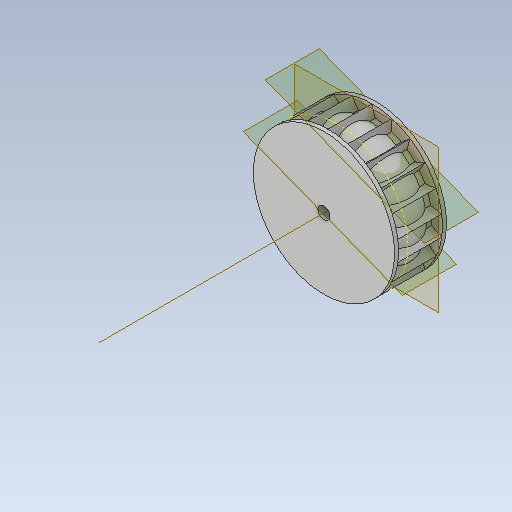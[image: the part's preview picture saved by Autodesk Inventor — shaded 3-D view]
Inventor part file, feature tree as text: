
AUTODESK INVENTOR PART (.ipt)
format: ipt  version: 2020 (Build 240168000, 168)  size: 521,216 bytes
history: native  units: mm
features: sketch x10, plane x5, other x4
ambient origin geometry x8: Origin, YZ Plane, XZ Plane, XY Plane, X Axis, Y Axis, Z Axis, Center Point
bodies: Solid1 (feature_tree)
feature tree (19):
  other  "front-wheel-new.ipt"
  other  "Solid1::front-wheel-new.ipt"
  other  "TaggingFeature1"
  sketch  "Sketch1"  dims[d0=10.0mm]
  sketch  "Sketch2"
  sketch  "Sketch3"
  sketch  "Sketch6"
  sketch  "Sketch7"
  sketch  "Sketch8"
  sketch  "Sketch10"
  sketch  "Sketch12"
  sketch  "Sketch13"
  sketch  "Sketch14"
  plane  "Work Plane1"
  plane  "Work Plane2"
  plane  "Work Plane3"
  plane  "Work Plane4"
  plane  "Work Plane5"
  other  "Work Axis1"
